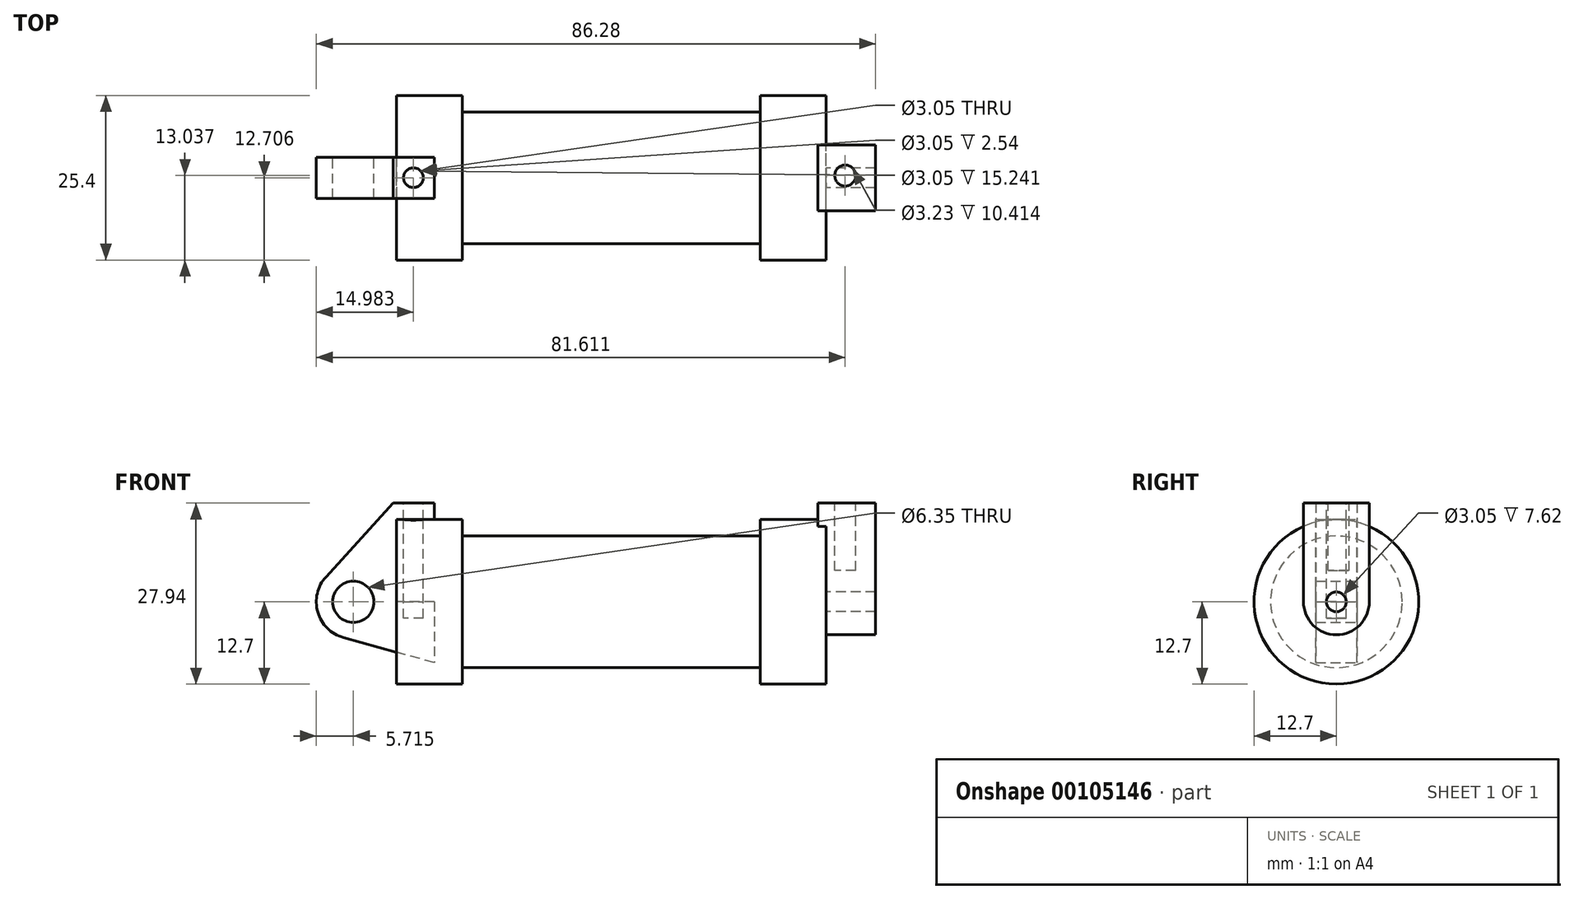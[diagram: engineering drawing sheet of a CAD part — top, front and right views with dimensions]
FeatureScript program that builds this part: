
annotation { "Feature Type Name" : "Feature", "Feature Type Description" : "" }
export const myFeature = defineFeature(function(context is Context, id is Id, definition is map)
    precondition{}
    {
        {
            var Q0;
            Q0=qCreatedBy(makeId("Front.planeOp"),FACE);
            var sketch = newSketch(context, id + "F0", { "sketchPlane" : qUnion([Q0])});
            skLineSegment(sketch, "E0", {"start": v(0, 0) * mm, "end": v(0, 12.7) * mm});
            skLineSegment(sketch, "E1", {"start": v(0, 12.7) * mm, "end": v(10.16, 12.7) * mm});
            skLineSegment(sketch, "E2", {"start": v(10.16, 12.7) * mm, "end": v(10.16, 10.16) * mm});
            skLineSegment(sketch, "E3", {"start": v(10.16, 10.16) * mm, "end": v(56.13, 10.16) * mm});
            skLineSegment(sketch, "E4", {"start": v(56.13, 10.16) * mm, "end": v(56.13, 12.7) * mm});
            skLineSegment(sketch, "E5", {"start": v(56.13, 12.7) * mm, "end": v(66.3, 12.7) * mm});
            skLineSegment(sketch, "E6", {"start": v(66.3, 12.7) * mm, "end": v(66.3, 0) * mm});
            skLineSegment(sketch, "E7", {"start": v(66.3, 0) * mm, "end": v(0, 0) * mm});
            skLineSegment(sketch, "E8", {"start": v(5.84, 15.24) * mm, "end": v(-0.5, 15.24) * mm});
            skLineSegment(sketch, "E9", {"start": v(-0.5, 15.24) * mm, "end": v(-10.88, 3.85) * mm});
            skLineSegment(sketch, "E10", {"start": v(0, 0) * mm, "end": v(-6.65, 0) * mm});
            skCircle(sketch, "E11", {"center": v(-6.65, 0) * mm, "radius": 5.72 * mm});
            skCircle(sketch, "E12", {"center": v(-6.65, 0) * mm, "radius": 3.18 * mm});
            skLineSegment(sketch, "E13", {"start": v(5.84, 15.24) * mm, "end": v(5.84, -9.4) * mm});
            skLineSegment(sketch, "E14", {"start": v(5.84, -9.4) * mm, "end": v(-8.18, -5.5) * mm});
            skSolve(sketch);
        }
        {
            var Q0;
            {var subQ0=sQuery(id+"F0.wireOp",EDGE,"E2");Q0=makeQuery(id+"F0.imprint","IMPRINT",FACE,{"disambiguationData":[TD([[makeQuery(id+"F0.imprint","IMPRINT",EDGE,{"derivedFrom":subQ0}),-1.0]])]});}
            var Q1;
            {var subQ0=sQuery(id+"F0.wireOp",EDGE,"E0");Q1=makeQuery(id+"F0.imprint","IMPRINT",FACE,{"disambiguationData":[TD([[makeQuery(id+"F0.imprint","IMPRINT",EDGE,{"derivedFrom":subQ0}),-1.0]])]});}
            var Q2;
            Q2=sQuery(id+"F0.wireOp",EDGE,"E7");
            revolve(context, id + "F1", {"entities" : qUnion([Q0, Q1]), "axis" : qUnion([Q2]), "revolveType" : RevolveType.FULL});
        }
        {
            var Q0;
            {var subQ4=sQuery(id+"F0.wireOp",EDGE,"E12");Q0=makeQuery(id+"F0.imprint","IMPRINT",FACE,{"disambiguationData":[TD([[makeQuery(id+"F0.imprint","IMPRINT",EDGE,{"derivedFrom":subQ4}),-1.0]])]});}
            var Q1;
            {var subQ3=sQuery(id+"F0.wireOp",EDGE,"E0");Q1=makeQuery(id+"F0.imprint","IMPRINT",FACE,{"disambiguationData":[TD([[makeQuery(id+"F0.imprint","IMPRINT",EDGE,{"derivedFrom":subQ3}),1.0]])]});}
            var Q2;
            {var subQ0=sQuery(id+"F0.wireOp",EDGE,"E14");Q2=makeQuery(id+"F0.imprint","IMPRINT",FACE,{"disambiguationData":[TD([[makeQuery(id+"F0.imprint","IMPRINT",EDGE,{"derivedFrom":subQ0}),-1.0]])]});}
            extrude(context, id + "F2", {"entities" : qUnion([Q0, Q1, Q2]), "endBound" : BoundingType.SYMMETRIC, "depth" : 6.35 * mm});
        }
        {
            var Q0;
            Q0=makeQuery(id+"F1.opRevolve","SWEPT_FACE",FACE,{"disambiguationData":[OSD([sQuery(id+"F0.wireOp",EDGE,"E6")])]});
            var sketch = newSketch(context, id + "F3", { "sketchPlane" : qUnion([Q0])});
            skCircle(sketch, "E15", {"center": v(0, 0) * mm, "radius": 1.52 * mm});
            skCircle(sketch, "E16", {"center": v(0, 0) * mm, "radius": 5.08 * mm});
            skLineSegment(sketch, "E17", {"start": v(-5.08, 0) * mm, "end": v(-5.08, 15.24) * mm});
            skLineSegment(sketch, "E18", {"start": v(5.08, 15.24) * mm, "end": v(5.08, 0) * mm});
            skLineSegment(sketch, "E19", {"start": v(-5.08, 15.24) * mm, "end": v(5.08, 15.24) * mm});
            skSolve(sketch);
        }
        {
            var Q0;
            Q0=makeQuery(id+"F3.imprint","IMPRINT",FACE,{"disambiguationData":[TD([[makeQuery(id+"F3.imprint","IMPRINT",EDGE,{"derivedFrom":sQuery(id+"F3.wireOp",EDGE,"E15")}),-1.0]])]});
            var Q1;
            {var subQ0=sQuery(id+"F3.wireOp",EDGE,"E17");var subQ1=sQuery(id+"F3.wireOp",EDGE,"E16");var subQ2=makeQuery(id+"F3.imprint","INTERSECT",VERTEX,{"derivedFrom":[subQ1,subQ0]});Q1=makeQuery(id+"F3.imprint","IMPRINT",FACE,{"disambiguationData":[TD([[makeQuery(id+"F3.imprint","IMPRINT",EDGE,{"disambiguationData":[TD([[subQ2,1.0]])],"derivedFrom":subQ1}),-1.0]])]});}
            var Q2;
            {var subQ0=sQuery(id+"F3.wireOp",EDGE,"E19");Q2=makeQuery(id+"F3.imprint","IMPRINT",FACE,{"disambiguationData":[TD([[makeQuery(id+"F3.imprint","IMPRINT",EDGE,{"derivedFrom":subQ0}),-1.0]])]});}
            extrude(context, id + "F4", {"entities" : qUnion([Q0, Q1, Q2]), "operationType" : NewBodyOperationType.ADD, "depth" : 7.62 * mm});
        }
        {
            var Q0;
            Q0=makeQuery(id+"F4.opExtrude","CAP_FACE",FACE,{"disambiguationData":[OSD([sQuery(id+"F3.wireOp",EDGE,"E15"),sQuery(id+"F3.wireOp",EDGE,"E16"),sQuery(id+"F3.wireOp",EDGE,"E17"),sQuery(id+"F3.wireOp",EDGE,"E18"),sQuery(id+"F3.wireOp",EDGE,"E19")])],"isStart":true});
            extrude(context, id + "F5", {"entities" : qUnion([Q0]), "operationType" : NewBodyOperationType.ADD, "depth" : 1.27 * mm});
        }
        {
            var Q0;
            Q0=makeQuery(id+"F2.opExtrude","SWEPT_FACE",FACE,{"disambiguationData":[OSD([sQuery(id+"F0.wireOp",EDGE,"E8")])]});
            var sketch = newSketch(context, id + "F6", { "sketchPlane" : qUnion([Q0])});
            skCircle(sketch, "E20", {"center": v(2.61, 0) * mm, "radius": 1.52 * mm});
            skCircle(sketch, "E21", {"center": v(69.45, 0.01) * mm, "radius": 1.52 * mm});
            skSolve(sketch);
        }
        {
            var Q0;
            Q0=makeQuery(id+"F6.imprint","IMPRINT",FACE,{"disambiguationData":[TD([[makeQuery(id+"F6.imprint","IMPRINT",EDGE,{"derivedFrom":sQuery(id+"F6.wireOp",EDGE,"E20")}),1.0]])]});
            extrude(context, id + "F7", {"entities" : qUnion([Q0]), "operationType" : NewBodyOperationType.REMOVE, "oppositeDirection" : true, "depth" : 17.78 * mm});
        }
        {
            var Q0;
            {var subQ0=sQuery(id+"F3.wireOp",EDGE,"E19");Q0=makeQuery(id+"F5.boolean.opBoolean","MERGE",FACE,{"derivedFrom":[makeQuery(id+"F4.opExtrude","SWEPT_FACE",FACE,{"disambiguationData":[OSD([subQ0])]}),makeQuery(id+"F5.opExtrude","SWEPT_FACE",FACE,{"disambiguationData":[OSD([subQ0])]})]});}
            var sketch = newSketch(context, id + "F8", { "sketchPlane" : qUnion([Q0])});
            skCircle(sketch, "E22", {"center": v(69.24, 0.34) * mm, "radius": 1.61 * mm});
            skSolve(sketch);
        }
        {
            var Q0;
            Q0=makeQuery(id+"F8.imprint","IMPRINT",FACE,{"disambiguationData":[TD([[makeQuery(id+"F8.imprint","IMPRINT",EDGE,{"derivedFrom":sQuery(id+"F8.wireOp",EDGE,"E22")}),1.0]])]});
            extrude(context, id + "F9", {"entities" : qUnion([Q0]), "operationType" : NewBodyOperationType.REMOVE, "oppositeDirection" : true, "depth" : 10.4 * mm});
        }
    });
